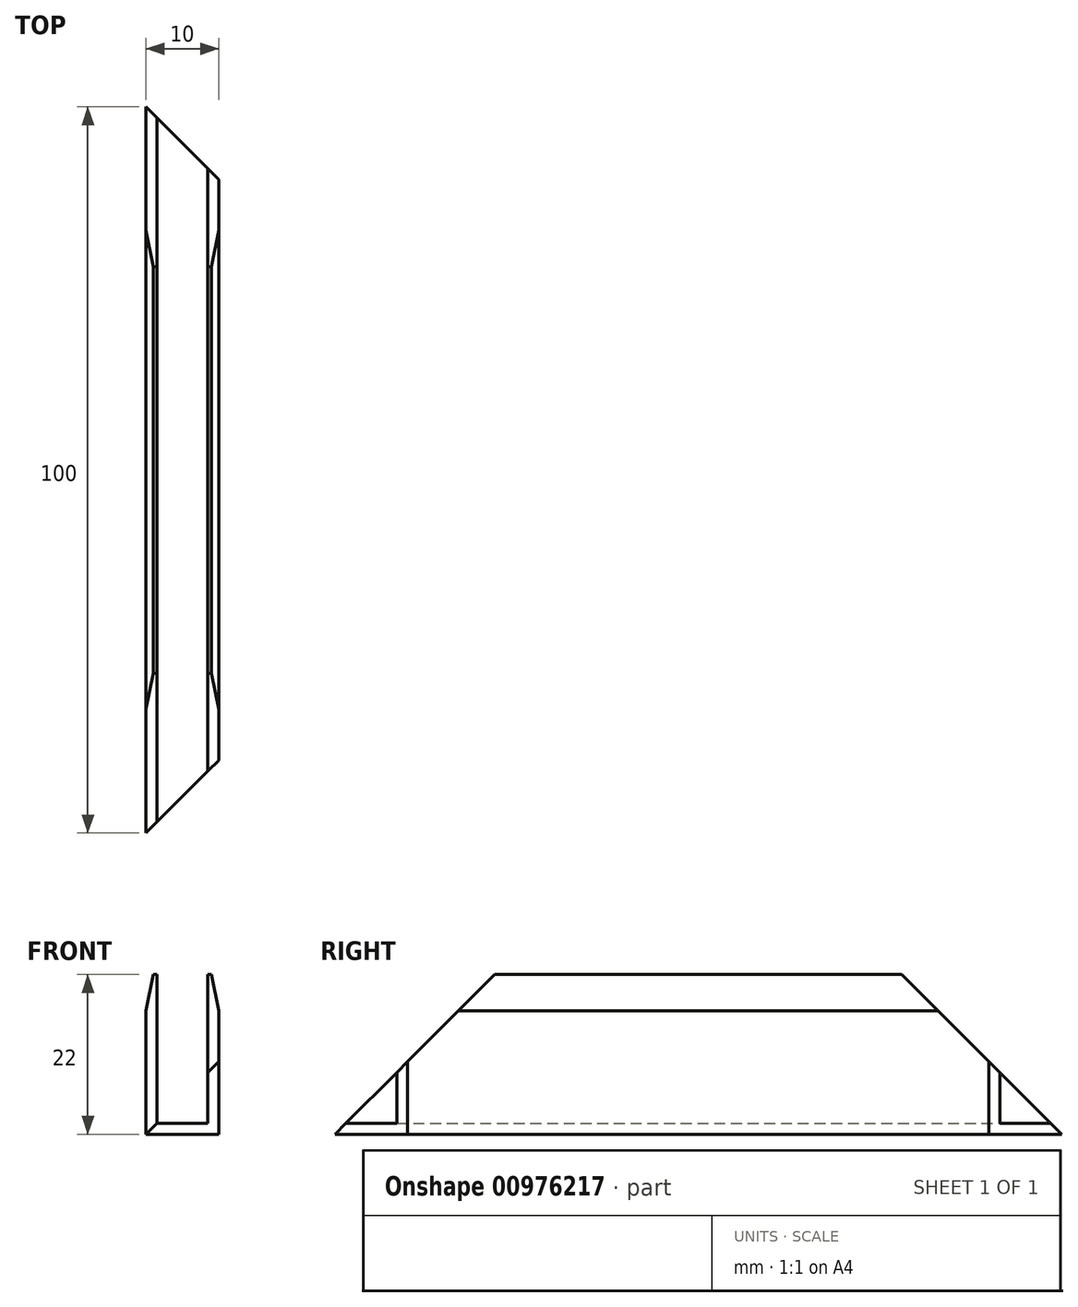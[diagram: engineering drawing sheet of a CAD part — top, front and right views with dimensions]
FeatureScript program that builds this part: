
annotation { "Feature Type Name" : "Feature", "Feature Type Description" : "" }
export const myFeature = defineFeature(function(context is Context, id is Id, definition is map)
    precondition{}
    {
        {
            var Q0;
            Q0=qCreatedBy(makeId("Front.planeOp"),FACE);
            var sketch = newSketch(context, id + "F0", { "sketchPlane" : qUnion([Q0])});
            skLineSegment(sketch, "E0.bottom", {"start": v(5, 11) * mm, "end": v(-5, 11) * mm});
            skLineSegment(sketch, "E0.top", {"start": v(5, -11) * mm, "end": v(-5, -11) * mm});
            skLineSegment(sketch, "E0.left", {"start": v(5, 11) * mm, "end": v(5, -11) * mm});
            skLineSegment(sketch, "E0.right", {"start": v(-5, 11) * mm, "end": v(-5, -11) * mm});
            skPoint(sketch, "E0.middle", {"position": v(0, 0) * mm});
            skSolve(sketch);
        }
        {
            var Q0;
            Q0=makeQuery(id+"F0.imprint","IMPRINT",FACE,{"disambiguationData":[TD([[makeQuery(id+"F0.imprint","IMPRINT",EDGE,{"derivedFrom":sQuery(id+"F0.wireOp",EDGE,"E0.bottom")}),1.0]])]});
            extrude(context, id + "F1", {"entities" : qUnion([Q0]), "endBound" : BoundingType.SYMMETRIC, "depth" : 100 * mm, "offsetDistance" : 25 * mm});
        }
        {
            var Q0;
            Q0=makeQuery(id+"F1.opExtrude","SWEPT_FACE",FACE,{"disambiguationData":[OSD([sQuery(id+"F0.wireOp",EDGE,"E0.bottom")])]});
            var Q1;
            Q1=makeQuery(id+"F1.opExtrude","CAP_FACE",FACE,{"disambiguationData":[OSD([sQuery(id+"F0.wireOp",EDGE,"E0.bottom"),sQuery(id+"F0.wireOp",EDGE,"E0.top"),sQuery(id+"F0.wireOp",EDGE,"E0.left"),sQuery(id+"F0.wireOp",EDGE,"E0.right")])],"isStart":false});
            var Q2;
            Q2=makeQuery(id+"F1.opExtrude","CAP_FACE",FACE,{"disambiguationData":[OSD([sQuery(id+"F0.wireOp",EDGE,"E0.bottom"),sQuery(id+"F0.wireOp",EDGE,"E0.top"),sQuery(id+"F0.wireOp",EDGE,"E0.left"),sQuery(id+"F0.wireOp",EDGE,"E0.right")])],"isStart":true});
            shell(context, id + "F2", {"entities" : qUnion([Q0, Q1, Q2]), "thickness" : 1.5 * mm});
        }
        {
            var Q0;
            Q0=makeQuery(id+"F1.opExtrude","SWEPT_EDGE",EDGE,{"disambiguationData":[OSD([sQuery(id+"F0.wireOp",EDGE,"E0.bottom"),sQuery(id+"F0.wireOp",EDGE,"E0.left")])]});
            chamfer(context, id + "F3", {"entities" : qUnion([Q0]), "chamferType" : ChamferType.TWO_OFFSETS, "width1" : 1 * mm, "oppositeDirection" : false, "width2" : 5 * mm, "tangentPropagation" : true});
        }
        {
            var Q0;
            Q0=makeQuery(id+"F1.opExtrude","SWEPT_EDGE",EDGE,{"disambiguationData":[OSD([sQuery(id+"F0.wireOp",EDGE,"E0.bottom"),sQuery(id+"F0.wireOp",EDGE,"E0.right")])]});
            chamfer(context, id + "F4", {"entities" : qUnion([Q0]), "chamferType" : ChamferType.TWO_OFFSETS, "width1" : 5 * mm, "oppositeDirection" : false, "width2" : 1 * mm, "tangentPropagation" : true});
        }
        {
            var Q0;
            Q0=qCreatedBy(makeId("Right.planeOp"),FACE);
            var sketch = newSketch(context, id + "F5", { "sketchPlane" : qUnion([Q0])});
            skLineSegment(sketch, "E1", {"start": v(-50, -11) * mm, "end": v(-28, 11) * mm});
            skLineSegment(sketch, "E2", {"start": v(-28, 11) * mm, "end": v(-50, 11) * mm});
            skLineSegment(sketch, "E3", {"start": v(-50, 11) * mm, "end": v(-50, -11) * mm});
            skLineSegment(sketch, "E4", {"start": v(0, 0) * mm, "end": v(0, 26.8) * mm, "construction": true});
            skLineSegment(sketch, "E5.MirrorCS", {"start": v(50, 11) * mm, "end": v(50, -11) * mm});
            skLineSegment(sketch, "E6.MirrorCS", {"start": v(28, 11) * mm, "end": v(50, 11) * mm});
            skLineSegment(sketch, "E7.MirrorCS", {"start": v(50, -11) * mm, "end": v(28, 11) * mm});
            skSolve(sketch);
        }
        {
            var Q0;
            Q0 = qSketchRegion(id + "F5", true);
            extrude(context, id + "F6", {"entities" : qUnion([Q0]), "operationType" : NewBodyOperationType.REMOVE, "endBound" : BoundingType.SYMMETRIC, "oppositeDirection" : true, "depth" : 20 * mm, "offsetDistance" : 25 * mm});
        }
        {
            var Q0;
            Q0=qCreatedBy(makeId("Top.planeOp"),FACE);
            var sketch = newSketch(context, id + "F7", { "sketchPlane" : qUnion([Q0])});
            skLineSegment(sketch, "E8", {"start": v(-5, 50) * mm, "end": v(5, 50) * mm});
            skLineSegment(sketch, "E9", {"start": v(5, 50) * mm, "end": v(5, 40) * mm});
            skLineSegment(sketch, "E10", {"start": v(5, 40) * mm, "end": v(-5, 50) * mm});
            skLineSegment(sketch, "E11", {"start": v(0, 0) * mm, "end": v(28.74, 0) * mm, "construction": true});
            skLineSegment(sketch, "E12.MirrorCS", {"start": v(5, -50) * mm, "end": v(5, -40) * mm});
            skLineSegment(sketch, "E13.MirrorCS", {"start": v(5, -40) * mm, "end": v(-5, -50) * mm});
            skLineSegment(sketch, "E14.MirrorCS", {"start": v(-5, -50) * mm, "end": v(5, -50) * mm});
            skSolve(sketch);
        }
        {
            var Q0;
            Q0 = qSketchRegion(id + "F7", true);
            extrude(context, id + "F8", {"entities" : qUnion([Q0]), "operationType" : NewBodyOperationType.REMOVE, "endBound" : BoundingType.SYMMETRIC, "oppositeDirection" : true, "depth" : 40 * mm, "offsetDistance" : 25 * mm});
        }
    });
